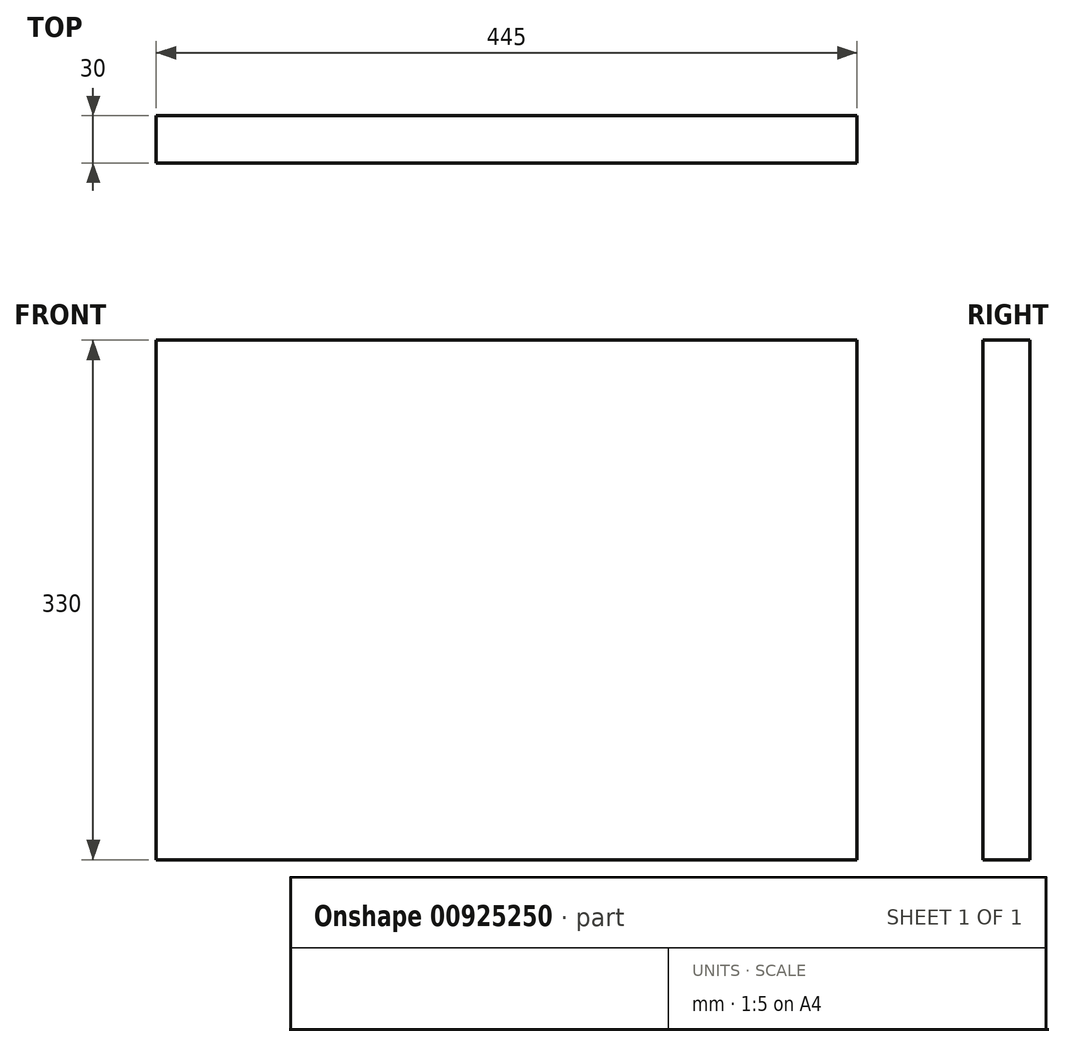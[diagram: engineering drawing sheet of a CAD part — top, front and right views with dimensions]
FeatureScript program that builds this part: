
annotation { "Feature Type Name" : "Feature", "Feature Type Description" : "" }
export const myFeature = defineFeature(function(context is Context, id is Id, definition is map)
    precondition{}
    {
        {
            var Q0;
            Q0=qCreatedBy(makeId("Front.planeOp"),FACE);
            var sketch = newSketch(context, id + "F0", { "sketchPlane" : qUnion([Q0])});
            skLineSegment(sketch, "E0.bottom", {"start": v(222.5, -165) * mm, "end": v(-222.5, -165) * mm});
            skLineSegment(sketch, "E0.top", {"start": v(222.5, 165) * mm, "end": v(-222.5, 165) * mm});
            skLineSegment(sketch, "E0.left", {"start": v(222.5, -165) * mm, "end": v(222.5, 165) * mm});
            skLineSegment(sketch, "E0.right", {"start": v(-222.5, -165) * mm, "end": v(-222.5, 165) * mm});
            skPoint(sketch, "E0.middle", {"position": v(0, 0) * mm});
            skSolve(sketch);
        }
        {
            var Q0;
            Q0=makeQuery(id+"F0.imprint","IMPRINT",FACE,{"disambiguationData":[TD([[makeQuery(id+"F0.imprint","IMPRINT",EDGE,{"derivedFrom":sQuery(id+"F0.wireOp",EDGE,"E0.bottom")}),-1.0]])]});
            extrude(context, id + "F1", {"entities" : qUnion([Q0]), "depth" : 30 * mm, "offsetDistance" : 25 * mm});
        }
    });
